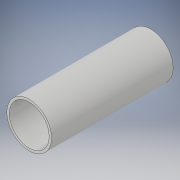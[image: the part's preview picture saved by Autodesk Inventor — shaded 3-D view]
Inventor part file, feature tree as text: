
AUTODESK INVENTOR PART (.ipt)
format: ipt  version: 2019 (Build 230136000, 136)  size: 98,816 bytes
history: native  units: mm
features: extrude x2, sketch x2
ambient origin geometry x8: Origin, YZ Plane, XZ Plane, XY Plane, X Axis, Y Axis, Z Axis, Center Point
bodies: Solid1 (feature_tree)
feature tree (4):
  extrude  "Extrusion1"  Depth=54.0mm TaperAngle=0.0deg
  extrude  "Extrusion2"  Depth=54.0mm TaperAngle=0.0deg
  sketch  "Sketch1"  dims[d0=19.87mm d1=54.0mm d2=0.0mm]
  sketch  "Sketch2"  dims[d3=17.72mm d4=54.0mm d5=0.0mm]
